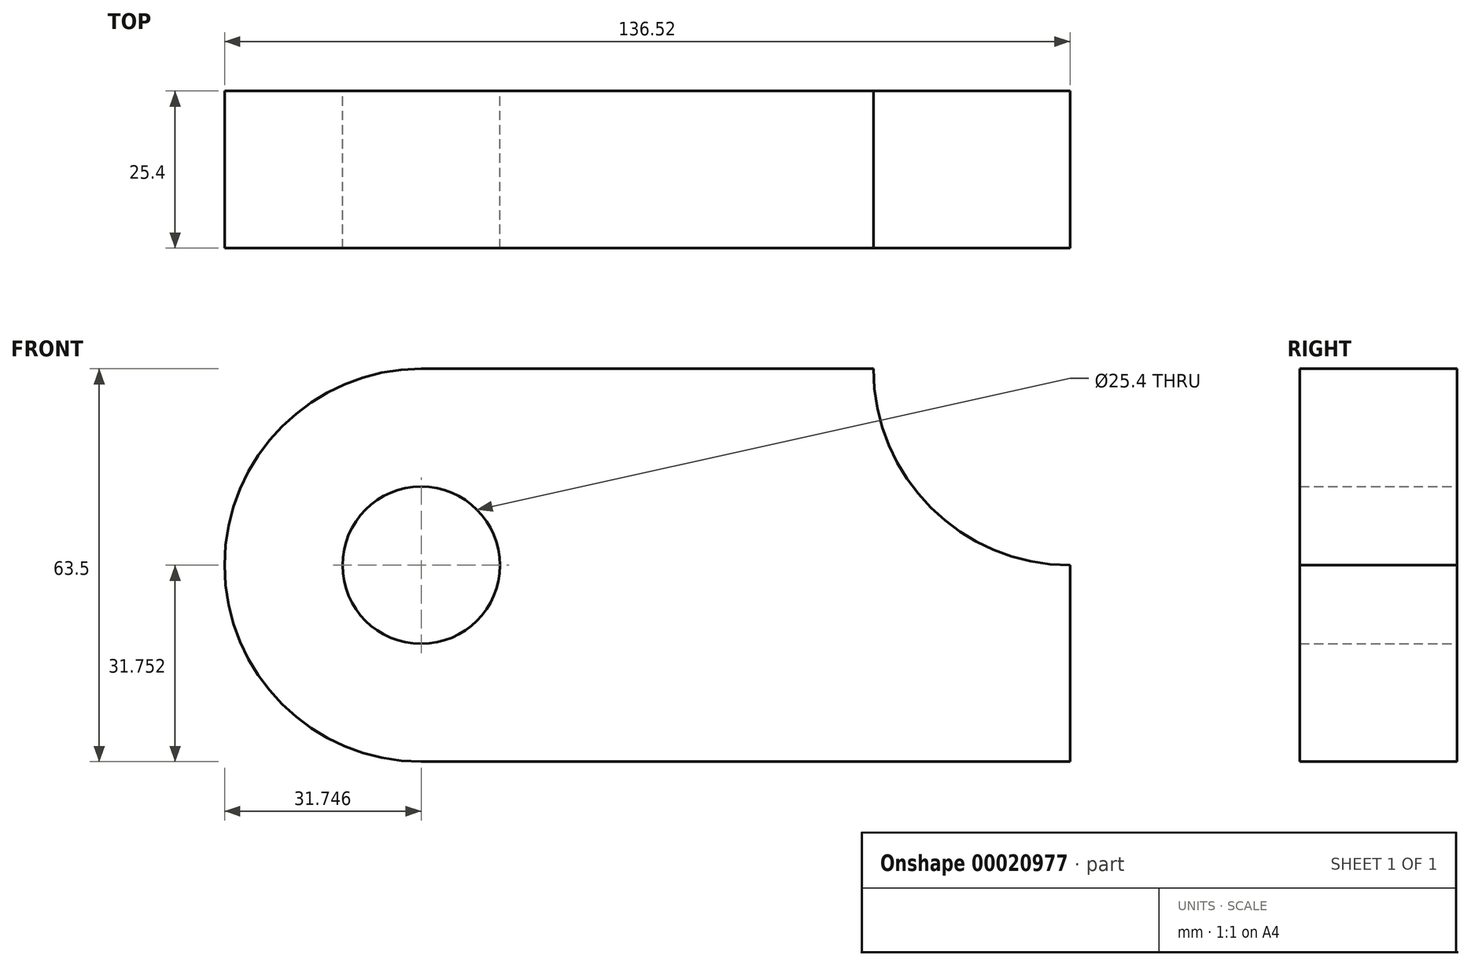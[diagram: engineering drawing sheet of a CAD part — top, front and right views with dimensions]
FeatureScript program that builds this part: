
annotation { "Feature Type Name" : "Feature", "Feature Type Description" : "" }
export const myFeature = defineFeature(function(context is Context, id is Id, definition is map)
    precondition{}
    {
        {
            var Q0;
            Q0=qCreatedBy(makeId("Front.planeOp"),FACE);
            var sketch = newSketch(context, id + "F0", { "sketchPlane" : qUnion([Q0])});
            skLineSegment(sketch, "E0.bottom", {"start": v(-72.13, 25.93) * mm, "end": v(32.64, 25.93) * mm});
            skLineSegment(sketch, "E0.top", {"start": v(-72.13, -37.57) * mm, "end": v(32.64, -37.57) * mm});
            skLineSegment(sketch, "E0.right", {"start": v(32.64, 25.93) * mm, "end": v(32.64, -37.57) * mm});
            skCircle(sketch, "E1", {"center": v(-72.13, -5.82) * mm, "radius": 31.75 * mm});
            skCircle(sketch, "E2", {"center": v(-72.13, -5.82) * mm, "radius": 12.7 * mm});
            skCircle(sketch, "E3", {"center": v(32.64, 25.93) * mm, "radius": 31.75 * mm});
            skSolve(sketch);
        }
        {
            var Q0;
            {var subQ6=sQuery(id+"F0.wireOp",EDGE,"E0.top");Q0=makeQuery(id+"F0.imprint","IMPRINT",FACE,{"disambiguationData":[TD([[makeQuery(id+"F0.imprint","IMPRINT",EDGE,{"derivedFrom":subQ6}),1.0]])]});}
            var Q1;
            Q1=makeQuery(id+"F0.imprint","IMPRINT",FACE,{"disambiguationData":[TD([[makeQuery(id+"F0.imprint","IMPRINT",EDGE,{"derivedFrom":sQuery(id+"F0.wireOp",EDGE,"E2")}),-1.0]])]});
            extrude(context, id + "F1", {"entities" : qUnion([Q0, Q1]), "depth" : 25.4 * mm});
        }
    });
